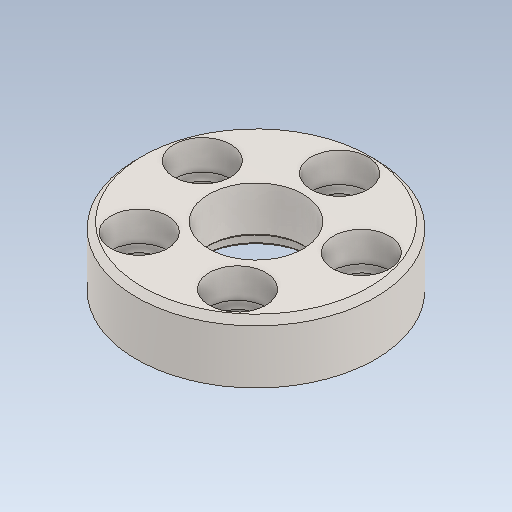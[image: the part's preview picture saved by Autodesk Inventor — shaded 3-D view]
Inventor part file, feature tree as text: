
AUTODESK INVENTOR PART (.ipt)
format: ipt  version: 2020 (Build 240168000, 168)  size: 155,136 bytes
history: native  units: in
note: dims shown in document units (in); Inventor stores cm internally (conversion verified against a paired STEP export)
features: chamfer x1
ambient origin geometry x8: Origin, YZ Plane, XZ Plane, XY Plane, X Axis, Y Axis, Z Axis, Center Point
bodies: Solid1 (feature_tree)
feature tree (1):
  chamfer  "Chamfer2"  [1 undecoded]
note: 1 required parameter value undecoded (feature->parameter linkage not recoverable at this tier; creation-order binding heuristic only, values carry confidence <= 0.55)
